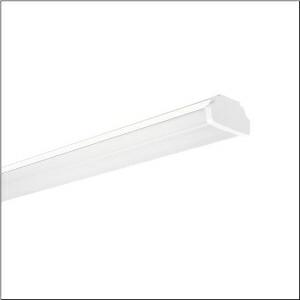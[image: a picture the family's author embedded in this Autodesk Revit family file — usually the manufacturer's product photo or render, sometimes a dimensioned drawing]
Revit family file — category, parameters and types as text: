
# Revit family: modario_r__31_mo_53bm81271v6080_691a
name_source: partatom
category: Lighting Fixtures
units: mm (PartAtom-declared; Revit-internal decimal feet)

## family parameters
Cut with Voids When Loaded = No
Host = Face
Light Source = No
Part Type = Normal
Room Calculation Point = No
Round Connector Dimension = Use Diameter
Shared = No

## types (1)
- Modario® 31 MO (1 x LED, 7820 lm, 50.8 W, 6500K)
    Apparent Load = 51 VA
    CIE Flux Codes = 47 80 95 92 100
    Color Rendering = 80
    Color Temperature = 6500K
    Default Elevation = 1800 mm
    Description = Modario® 31 MOluminaire insert, length: 1.495mm, width: 81mm, height: 82mm, LED rated luminous flux: 7.820lm, light colour: 865, control gear: ON/OFF, control gear: ECG, with plug, 3-pole, with phase selection, mains connection: 220..240V, AC, 50/60Hz, primary optical cover: cover, of PMMA, light emission: direct distribution, primary light characteristic: symmetric, protection rating (complete): IP20, protection rating (LED compartment): IP50, insulation class (complete): insulation class I (protective earthing), certification: CE, ENEC, VDE, permissible ambient temperature for indoor applications: -35..+35°C, corresponds to IFS (International Featured Standards) requirements for safety and quality in the food industry, reducing of maximum allowable ambient temperature of 5°C with ceiling mounting, packaging unit: 1 piece
    Height = 92 mm
    Lamp = 1 x LED
    Lamp Light Flux = 7820 lm
    Lamp Power = 50.8 W
    Lamp count = 1
    Length = 1495 mm
    Luminous efficacy = 154 lm/W
    Manufacturer = Siteco
    ModVariant = No
    Model = 53BM81271V6080
    Mounting Place = Ceiling
    Mounting Type = Pendant
    Number of Poles = 1
    OnlyDefault = Yes
    Power Factor = 1
    Product Name = Modario® 31 MO
    Product group = luminaire insert
    ProductGroupID = 902
    Protection Class = Protection class I
    Protection Degree = IP 20
    RLX_Detail_Level = 1
    RlxData = <blob elided: 38373 chars, md5=be419c93>
    Socket = socket
    Standby Power = 0 W
    System Light Flux = 7820 lm
    System Power = 51 W
    Type Comments = Product without accessories
    Type Image = l_1003447.jpg
    URL = http://relux.com
    VarID = ---
    Voltage = 0 V
    Weight = 0.00 kg
    Width = 81 mm

## geometry (parser evidence)
native form markers: Blend x4, Sweep x10
no freeform markers — native parametric forms only
